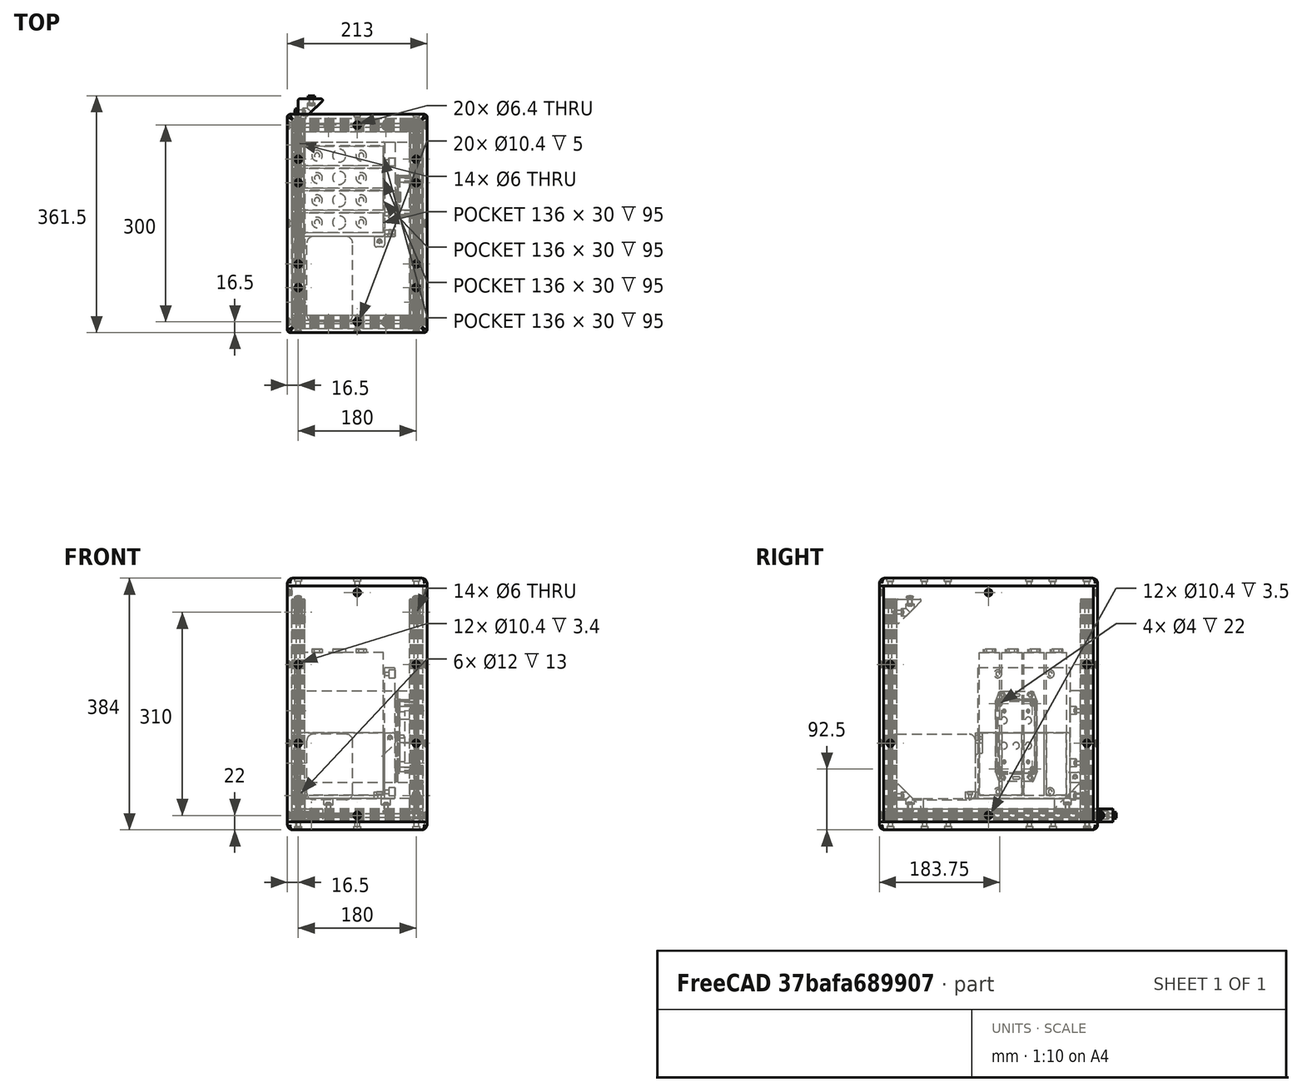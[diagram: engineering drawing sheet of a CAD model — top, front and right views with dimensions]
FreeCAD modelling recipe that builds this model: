
FCSTD DOCUMENT  (FreeCAD 0.17R9796 (Git))
Label: UPKframeNG2f
License: All rights reserved
LicenseURL: http://en.wikipedia.org/wiki/All_rights_reserved
objects: Part::Feature×70, Part::FeaturePython×24, Part::Compound×12, App::FeaturePython×8, App::Part×6, Part::Cylinder×5, Part::Box×4, Part::Cut×4, PartDesign::Body×2, PartDesign::Pocket×1, Part::Fillet×1, Part::MultiFuse×1
note: 125 computed .brp shape members not serialized (recipe doc carries the construction recipe); baked Part::Feature solids carry a one-line shape summary decoded from their .brp

FEATURE [Part::Feature] Pocket003001  label="tslot32con"
  Placement = pos=(0,10,10) rot=(1,0,0;1.5708rad)
  shape: bbox 20 x 320 x 20 mm, 150 faces (baked)
FEATURE [Part::Feature] Pocket003002  label="tslot16"
  Placement = pos=(10,0,10) rot=(0,1,0;1.5708rad)
  shape: bbox 160 x 20 x 20 mm, 94 faces (baked)
FEATURE [Part::Feature] Pocket003006  label="tslot16_001"
  Placement = pos=(10,-300,10) rot=(0,1,0;1.5708rad)
  shape: bbox 160 x 20 x 20 mm, 94 faces (baked)
FEATURE [Part::Feature] Pocket003007  label="tslot32con_001"
  Placement = pos=(180,-310,10) rot=(0,0.707107,0.707107;3.14159rad)
  shape: bbox 20 x 320 x 20 mm, 150 faces (baked)
FEATURE [Part::FeaturePython] Screw  label="M6x25-Screw"  # Fasteners workbench fastener (typed FeaturePython)
  Placement = pos=(-4,0,10) rot=(0,-1,0;1.5708rad)
  diameter = 7
  invert = false
  length = 6
  matchOuter = false
  offset = 0
  thread = false
  type = 15
FEATURE [Part::FeaturePython] Screw001  label="M6x25-Screw004"  # Fasteners workbench fastener (typed FeaturePython)
  Placement = pos=(-4,-300,10) rot=(0,-1,0;1.5708rad)
  diameter = 7
  invert = false
  length = 6
  matchOuter = false
  offset = 0
  thread = false
  type = 15
FEATURE [Part::FeaturePython] Screw002  label="M6x25-Screw005"  # Fasteners workbench fastener (typed FeaturePython)
  Placement = pos=(184,0,10) rot=(0,1,0;1.5708rad)
  diameter = 7
  invert = false
  length = 6
  matchOuter = false
  offset = 0
  thread = false
  type = 15
FEATURE [Part::FeaturePython] Screw004  label="M6x25-Screw006"  # Fasteners workbench fastener (typed FeaturePython)
  Placement = pos=(184,-300,10) rot=(0,1,0;1.5708rad)
  diameter = 7
  invert = false
  length = 6
  matchOuter = false
  offset = 0
  thread = false
  type = 15
FEATURE [App::Part] Part  label="lower_frame"
  Group = -> [Pocket003001,Pocket003002,Pocket003006,Pocket003007,Screw,Screw001,Screw002,Screw004]
  License = CC BY 3.0
  LicenseURL = http://creativecommons.org/licenses/by/3.0/
  Origin = -> PartOrigin
FEATURE [Part::Feature] Pocket003008  label="tslot32con001"
  Placement = pos=(0,10,10) rot=(1,0,0;1.5708rad)
  shape: bbox 20 x 320 x 20 mm, 150 faces (baked)
FEATURE [Part::Feature] Pocket003009  label="tslot041"
  Placement = pos=(10,0,10) rot=(0,1,0;1.5708rad)
  shape: bbox 160 x 20 x 20 mm, 94 faces (baked)
FEATURE [Part::Feature] Pocket003010  label="tslot16_002"
  Placement = pos=(10,-300,10) rot=(0,1,0;1.5708rad)
  shape: bbox 160 x 20 x 20 mm, 94 faces (baked)
FEATURE [Part::Feature] Pocket003011  label="tslot32con_002"
  Placement = pos=(180,-310,10) rot=(0,0.707107,0.707107;3.14159rad)
  shape: bbox 20 x 320 x 20 mm, 150 faces (baked)
FEATURE [Part::FeaturePython] Screw005  label="M6x25-Screw007"  # Fasteners workbench fastener (typed FeaturePython)
  Placement = pos=(-4,0,10) rot=(0,-1,0;1.5708rad)
  diameter = 7
  invert = false
  length = 6
  matchOuter = false
  offset = 0
  thread = false
  type = 15
FEATURE [Part::FeaturePython] Screw006  label="M6x25-Screw008"  # Fasteners workbench fastener (typed FeaturePython)
  Placement = pos=(-4,-300,10) rot=(0,-1,0;1.5708rad)
  diameter = 7
  invert = false
  length = 6
  matchOuter = false
  offset = 0
  thread = false
  type = 15
FEATURE [Part::FeaturePython] Screw007  label="M6x25-Screw009"  # Fasteners workbench fastener (typed FeaturePython)
  Placement = pos=(184,0,10) rot=(0,1,0;1.5708rad)
  diameter = 7
  invert = false
  length = 6
  matchOuter = false
  offset = 0
  thread = false
  type = 15
FEATURE [Part::FeaturePython] Screw008  label="M6x25-Screw010"  # Fasteners workbench fastener (typed FeaturePython)
  Placement = pos=(184,-300,10) rot=(0,1,0;1.5708rad)
  diameter = 7
  invert = false
  length = 6
  matchOuter = false
  offset = 0
  thread = false
  type = 15
FEATURE [App::Part] Part001  label="upper_frame"
  Group = -> [Pocket003008,Pocket003009,Pocket003010,Pocket003011,Screw005,Screw006,Screw007,Screw008]
  License = CC BY 3.0
  LicenseURL = http://creativecommons.org/licenses/by/3.0/
  Origin = -> PartOrigin001
  Placement = pos=(0,0,340) rot=(0,0,1;0rad)
FEATURE [Part::Feature] Fillet004001  label="Fillet005"
  shape: bbox 37.5 x 37.5 x 20 mm, 26 faces (baked)
FEATURE [Part::FeaturePython] Screw009  label="M6x12-Screw"  # Fasteners workbench fastener (typed FeaturePython)
  Placement = pos=(7,20,10) rot=(0,1,0;1.5708rad)
  diameter = 4
  invert = false
  length = 1
  matchOuter = false
  offset = 0
  thread = false
  type = 20
FEATURE [Part::Feature] Body001  label="m6nutplate"
  Placement = pos=(-1.5,15,5) rot=(0,-1,0;1.5708rad)
  shape: bbox 3 x 10 x 10 mm, 9 faces (baked)
FEATURE [App::Part] Part002  label="cornerstonescrewnut"
  License = CC BY 3.0
  LicenseURL = http://creativecommons.org/licenses/by/3.0/
  Origin = -> PartOrigin002
  Placement = pos=(10,-50,20) rot=(0,-1,0;1.5708rad)
FEATURE [Part::FeaturePython] Screw010  label="M6x12-Screw001"  # Fasteners workbench fastener (typed FeaturePython)
  Placement = pos=(20,33,10) rot=(1,0,0;1.5708rad)
  diameter = 4
  invert = false
  length = 1
  matchOuter = false
  offset = 0
  thread = false
  type = 20
FEATURE [Part::Feature] Body002  label="m6nutplate001"
  Placement = pos=(15,41.5,5) rot=(0.57735,0.57735,0.57735;4.18879rad)
  shape: bbox 10 x 3 x 10 mm, 9 faces (baked)
FEATURE [Part::Feature] Fillet004002  label="Fillet006"
  shape: bbox 37.5 x 37.5 x 20 mm, 26 faces (baked)
FEATURE [Part::FeaturePython] Screw011  label="M6x12-Screw002"  # Fasteners workbench fastener (typed FeaturePython)
  Placement = pos=(7,20,10) rot=(0,1,0;1.5708rad)
  diameter = 4
  invert = false
  length = 1
  matchOuter = false
  offset = 0
  thread = false
  type = 20
FEATURE [Part::Feature] Body003  label="m6nutplate002"
  Placement = pos=(-1.5,15,5) rot=(0,-1,0;1.5708rad)
  shape: bbox 3 x 10 x 10 mm, 9 faces (baked)
FEATURE [Part::FeaturePython] Screw012  label="M6x12-Screw003"  # Fasteners workbench fastener (typed FeaturePython)
  Placement = pos=(20,33,10) rot=(1,0,0;1.5708rad)
  diameter = 4
  invert = false
  length = 1
  matchOuter = false
  offset = 0
  thread = false
  type = 20
FEATURE [Part::Feature] Body004  label="m6nutplate003"
  Placement = pos=(15,41.5,5) rot=(0.57735,0.57735,0.57735;4.18879rad)
  shape: bbox 10 x 3 x 10 mm, 9 faces (baked)
FEATURE [App::Part] Part003  label="cornerstonescrewnut001"
  Group = -> [Body003,Screw011,Fillet004002,Screw012,Body004,PartOrigin002,Body001,Screw009,Fillet004001,Screw010,Body002,Part002]
  License = CC BY 3.0
  LicenseURL = http://creativecommons.org/licenses/by/3.0/
  Origin = -> PartOrigin003
  Placement = pos=(190,-50,20) rot=(0,-1,0;1.5708rad)
FEATURE [Part::Feature] Fillet004003  label="Fillet007"
  shape: bbox 37.5 x 37.5 x 20 mm, 26 faces (baked)
FEATURE [Part::FeaturePython] Screw013  label="M6x12-Screw004"  # Fasteners workbench fastener (typed FeaturePython)
  Placement = pos=(7,20,10) rot=(0,1,0;1.5708rad)
  diameter = 4
  invert = false
  length = 1
  matchOuter = false
  offset = 0
  thread = false
  type = 20
FEATURE [Part::Feature] Body005  label="m6nutplate004"
  Placement = pos=(-1.5,15,5) rot=(0,-1,0;1.5708rad)
  shape: bbox 3 x 10 x 10 mm, 9 faces (baked)
FEATURE [Part::FeaturePython] Screw014  label="M6x12-Screw005"  # Fasteners workbench fastener (typed FeaturePython)
  Placement = pos=(20,33,10) rot=(1,0,0;1.5708rad)
  diameter = 4
  invert = false
  length = 1
  matchOuter = false
  offset = 0
  thread = false
  type = 20
FEATURE [Part::Feature] Body006  label="m6nutplate005"
  Placement = pos=(15,41.5,5) rot=(0.57735,0.57735,0.57735;4.18879rad)
  shape: bbox 10 x 3 x 10 mm, 9 faces (baked)
FEATURE [App::Part] Part004  label="cornerstonescrewnut002"
  Group = -> [Body005,Screw013,Fillet004003,Screw014,Body006]
  License = CC BY 3.0
  LicenseURL = http://creativecommons.org/licenses/by/3.0/
  Origin = -> PartOrigin004
  Placement = pos=(-10,-50,340) rot=(0,1,0;1.5708rad)
FEATURE [Part::Feature] Fillet004004  label="Fillet008"
  shape: bbox 37.5 x 37.5 x 20 mm, 26 faces (baked)
FEATURE [Part::FeaturePython] Screw015  label="M6x12-Screw006"  # Fasteners workbench fastener (typed FeaturePython)
  Placement = pos=(7,20,10) rot=(0,1,0;1.5708rad)
  diameter = 4
  invert = false
  length = 1
  matchOuter = false
  offset = 0
  thread = false
  type = 20
FEATURE [Part::Feature] Body007  label="m6nutplate006"
  Placement = pos=(-1.5,15,5) rot=(0,-1,0;1.5708rad)
  shape: bbox 3 x 10 x 10 mm, 9 faces (baked)
FEATURE [Part::FeaturePython] Screw016  label="M6x12-Screw007"  # Fasteners workbench fastener (typed FeaturePython)
  Placement = pos=(20,33,10) rot=(1,0,0;1.5708rad)
  diameter = 4
  invert = false
  length = 1
  matchOuter = false
  offset = 0
  thread = false
  type = 20
FEATURE [Part::Feature] Body008  label="m6nutplate007"
  Placement = pos=(15,41.5,5) rot=(0.57735,0.57735,0.57735;4.18879rad)
  shape: bbox 10 x 3 x 10 mm, 9 faces (baked)
FEATURE [App::Part] Part005  label="cornerstonescrewnut003"
  Group = -> [Body007,Screw015,Fillet004004,Screw016,Body008]
  License = CC BY 3.0
  LicenseURL = http://creativecommons.org/licenses/by/3.0/
  Origin = -> PartOrigin005
  Placement = pos=(170,-50,340) rot=(0,1,0;1.5708rad)
FEATURE [Part::Feature] Body009001  label="m6nutplate010"
  Placement = pos=(-1.5,15,5) rot=(0,-1,0;1.5708rad)
  shape: bbox 3 x 10 x 10 mm, 9 faces (baked)
FEATURE [Part::Feature] Body010001  label="m6nutplate011"
  Placement = pos=(15,41.5,5) rot=(0.57735,0.57735,0.57735;4.18879rad)
  shape: bbox 10 x 3 x 10 mm, 9 faces (baked)
FEATURE [Part::Feature] Screw018001  label="M6x12-Screw010"
  Placement = pos=(20,33,10) rot=(1,0,0;1.5708rad)
  shape: bbox 10.5 x 15.3 x 10.5 mm, 15 faces (baked)
FEATURE [Part::Feature] Screw017001  label="M6x12-Screw011"
  Placement = pos=(7,20,10) rot=(0,1,0;1.5708rad)
  shape: bbox 15.3 x 10.5 x 10.5 mm, 15 faces (baked)
FEATURE [Part::Feature] Fillet004005001  label="Fillet010"
  shape: bbox 37.5 x 37.5 x 20 mm, 26 faces (baked)
FEATURE [Part::Compound] Compound
  Links = -> [Body009001,Fillet004005001,Screw017001,Body010001,Screw018001]
  Placement = pos=(10,-250,340) rot=(0.707107,0,-0.707107;3.14159rad)
FEATURE [Part::Feature] Body010002  label="m6nutplate012"
  Placement = pos=(-1.5,15,5) rot=(0,-1,0;1.5708rad)
  shape: bbox 3 x 10 x 10 mm, 9 faces (baked)
FEATURE [Part::Feature] Body010003  label="m6nutplate013"
  Placement = pos=(15,41.5,5) rot=(0.57735,0.57735,0.57735;4.18879rad)
  shape: bbox 10 x 3 x 10 mm, 9 faces (baked)
FEATURE [Part::Feature] Screw018002  label="M6x12-Screw012"
  Placement = pos=(20,33,10) rot=(1,0,0;1.5708rad)
  shape: bbox 10.5 x 15.3 x 10.5 mm, 15 faces (baked)
FEATURE [Part::Feature] Screw018003  label="M6x12-Screw013"
  Placement = pos=(7,20,10) rot=(0,1,0;1.5708rad)
  shape: bbox 15.3 x 10.5 x 10.5 mm, 15 faces (baked)
FEATURE [Part::Feature] Fillet004005002  label="Fillet011"
  shape: bbox 37.5 x 37.5 x 20 mm, 26 faces (baked)
FEATURE [Part::Compound] Compound001
  Links = -> [Body010002,Fillet004005002,Screw018003,Body010003,Screw018002]
  Placement = pos=(190,-250,340) rot=(0.707107,0,-0.707107;3.14159rad)
FEATURE [Part::Feature] Body010004  label="m6nutplate014"
  Placement = pos=(-1.5,15,5) rot=(0,-1,0;1.5708rad)
  shape: bbox 3 x 10 x 10 mm, 9 faces (baked)
FEATURE [Part::Feature] Body010005  label="m6nutplate015"
  Placement = pos=(15,41.5,5) rot=(0.57735,0.57735,0.57735;4.18879rad)
  shape: bbox 10 x 3 x 10 mm, 9 faces (baked)
FEATURE [Part::Feature] Screw018004  label="M6x12-Screw014"
  Placement = pos=(20,33,10) rot=(1,0,0;1.5708rad)
  shape: bbox 10.5 x 15.3 x 10.5 mm, 15 faces (baked)
FEATURE [Part::Feature] Screw018005  label="M6x12-Screw015"
  Placement = pos=(7,20,10) rot=(0,1,0;1.5708rad)
  shape: bbox 15.3 x 10.5 x 10.5 mm, 15 faces (baked)
FEATURE [Part::Feature] Fillet004005003  label="Fillet012"
  shape: bbox 37.5 x 37.5 x 20 mm, 26 faces (baked)
FEATURE [Part::Compound] Compound002
  Links = -> [Body010004,Fillet004005003,Screw018005,Body010005,Screw018004]
  Placement = pos=(10,-290,60) rot=(0.57735,0.57735,-0.57735;4.18879rad)
FEATURE [Part::Feature] Body010006  label="m6nutplate016"
  Placement = pos=(-1.5,15,5) rot=(0,-1,0;1.5708rad)
  shape: bbox 3 x 10 x 10 mm, 9 faces (baked)
FEATURE [Part::Feature] Body010007  label="m6nutplate017"
  Placement = pos=(15,41.5,5) rot=(0.57735,0.57735,0.57735;4.18879rad)
  shape: bbox 10 x 3 x 10 mm, 9 faces (baked)
FEATURE [Part::Feature] Screw018006  label="M6x12-Screw016"
  Placement = pos=(20,33,10) rot=(1,0,0;1.5708rad)
  shape: bbox 10.5 x 15.3 x 10.5 mm, 15 faces (baked)
FEATURE [Part::Feature] Screw018007  label="M6x12-Screw017"
  Placement = pos=(7,20,10) rot=(0,1,0;1.5708rad)
  shape: bbox 15.3 x 10.5 x 10.5 mm, 15 faces (baked)
FEATURE [Part::Feature] Fillet004005004  label="Fillet013"
  shape: bbox 37.5 x 37.5 x 20 mm, 26 faces (baked)
FEATURE [Part::Compound] Compound003
  Links = -> [Body010006,Fillet004005004,Screw018007,Body010007,Screw018006]
  Placement = pos=(190,-290,60) rot=(0.57735,0.57735,-0.57735;4.18879rad)
FEATURE [Part::Feature] Pocket001001  label="tslot32"
  Placement = pos=(0,0,20) rot=(0,0,1;0rad)
  shape: bbox 20 x 20 x 320 mm, 94 faces (baked)
FEATURE [Part::Feature] Body010008  label="m6nutplate018"
  Placement = pos=(-1.5,15,5) rot=(0,-1,0;1.5708rad)
  shape: bbox 3 x 10 x 10 mm, 9 faces (baked)
FEATURE [Part::Feature] Body010009  label="m6nutplate019"
  Placement = pos=(15,41.5,5) rot=(0.57735,0.57735,0.57735;4.18879rad)
  shape: bbox 10 x 3 x 10 mm, 9 faces (baked)
FEATURE [Part::Feature] Screw018008  label="M6x12-Screw018"
  Placement = pos=(20,33,10) rot=(1,0,0;1.5708rad)
  shape: bbox 10.5 x 15.3 x 10.5 mm, 15 faces (baked)
FEATURE [Part::Feature] Screw018009  label="M6x12-Screw019"
  Placement = pos=(7,20,10) rot=(0,1,0;1.5708rad)
  shape: bbox 15.3 x 10.5 x 10.5 mm, 15 faces (baked)
FEATURE [Part::Feature] Fillet004005005  label="Fillet014"
  shape: bbox 37.5 x 37.5 x 20 mm, 26 faces (baked)
FEATURE [Part::Compound] Compound004
  Links = -> [Body010008,Fillet004005005,Screw018009,Body010009,Screw018008]
  Placement = pos=(-10,-10,60) rot=(0.57735,-0.57735,0.57735;4.18879rad)
FEATURE [Part::Feature] Pocket003012  label="tslot32_001"
  Placement = pos=(0,-300,20) rot=(0,0,1;0rad)
  shape: bbox 20 x 20 x 320 mm, 94 faces (baked)
FEATURE [Part::Feature] Pocket003013  label="tslot32_002"
  Placement = pos=(180,0,20) rot=(0,0,1;0rad)
  shape: bbox 20 x 20 x 320 mm, 94 faces (baked)
FEATURE [Part::Feature] Pocket003014  label="tslot32_003"
  Placement = pos=(180,-300,20) rot=(0,0,1;0rad)
  shape: bbox 20 x 20 x 320 mm, 94 faces (baked)
FEATURE [PartDesign::Body] Body010027
FEATURE [Part::FeaturePython] Screw018021  label="M6x12-Screw032"  # Fasteners workbench fastener (typed FeaturePython)
  diameter = 4
  invert = false
  length = 1
  matchOuter = false
  offset = 0
  thread = false
  type = 20
FEATURE [Part::Feature] Body010028  label="m6nutplate032"
  Placement = pos=(5,-5,-8.39) rot=(0,1,0;3.14159rad)
  shape: bbox 10 x 10 x 3 mm, 9 faces (baked)
FEATURE [App::FeaturePython] circularEdgeConstraint009  # a2plus constraint (typed FeaturePython)
  Object1 = Screw
  Object2 = Body001
  SubElement1 = Edge7
  SubElement2 = Edge20
  Type = circularEdge
  directionConstraint = 1
  lockRotation = false
  offset = 0
FEATURE [Part::Compound] Compound017  label="nutplate12screw008"
  Links = -> [Screw018021,circularEdgeConstraint009,Body010028]
  Placement = pos=(10,30,6) rot=(0,0,1;0rad)
FEATURE [Part::FeaturePython] Screw018022  label="M6x12-Screw033"  # Fasteners workbench fastener (typed FeaturePython)
  diameter = 4
  invert = false
  length = 1
  matchOuter = false
  offset = 0
  thread = false
  type = 20
FEATURE [Part::Feature] Body010029  label="m6nutplate033"
  Placement = pos=(5,-5,-8.39) rot=(0,1,0;3.14159rad)
  shape: bbox 10 x 10 x 3 mm, 9 faces (baked)
FEATURE [App::FeaturePython] circularEdgeConstraint010  # a2plus constraint (typed FeaturePython)
  Object1 = Screw
  Object2 = Body001
  SubElement1 = Edge7
  SubElement2 = Edge20
  Type = circularEdge
  directionConstraint = 1
  lockRotation = false
  offset = 0
FEATURE [Part::Compound] Compound018  label="nutplate12screw009"
  Links = -> [Screw018022,circularEdgeConstraint010,Body010029]
  Placement = pos=(10,110,6) rot=(0,0,1;0rad)
FEATURE [Part::FeaturePython] Screw018023  label="M6x12-Screw034"  # Fasteners workbench fastener (typed FeaturePython)
  diameter = 4
  invert = false
  length = 1
  matchOuter = false
  offset = 0
  thread = false
  type = 20
FEATURE [Part::Feature] Body010030  label="m6nutplate034"
  Placement = pos=(5,-5,-8.39) rot=(0,1,0;3.14159rad)
  shape: bbox 10 x 10 x 3 mm, 9 faces (baked)
FEATURE [App::FeaturePython] circularEdgeConstraint011  # a2plus constraint (typed FeaturePython)
  Object1 = Screw
  Object2 = Body001
  SubElement1 = Edge7
  SubElement2 = Edge20
  Type = circularEdge
  directionConstraint = 1
  lockRotation = false
  offset = 0
FEATURE [Part::Compound] Compound019  label="nutplate12screw010"
  Links = -> [Screw018023,circularEdgeConstraint011,Body010030]
  Placement = pos=(190,110,6) rot=(0,0,1;0rad)
FEATURE [Part::FeaturePython] Screw018024  label="M6x12-Screw035"  # Fasteners workbench fastener (typed FeaturePython)
  diameter = 4
  invert = false
  length = 1
  matchOuter = false
  offset = 0
  thread = false
  type = 20
FEATURE [Part::Feature] Body010031  label="m6nutplate035"
  Placement = pos=(5,-5,-8.39) rot=(0,1,0;3.14159rad)
  shape: bbox 10 x 10 x 3 mm, 9 faces (baked)
FEATURE [App::FeaturePython] circularEdgeConstraint012  # a2plus constraint (typed FeaturePython)
  Object1 = Screw
  Object2 = Body001
  SubElement1 = Edge7
  SubElement2 = Edge20
  Type = circularEdge
  directionConstraint = 1
  lockRotation = false
  offset = 0
FEATURE [Part::Compound] Compound020  label="nutplate12screw011"
  Links = -> [Screw018024,circularEdgeConstraint012,Body010031]
  Placement = pos=(190,30,6) rot=(0,0,1;0rad)
FEATURE [Part::Compound] Compound021  label="front_plate"
  Links = -> [Body010027,Compound020,Compound019,Compound017,Compound018]
  Placement = pos=(-10,-10,60) rot=(1,0,0;1.5708rad)
FEATURE [Part::Compound] Compound016  label="bottom_plate"
  Placement = pos=(190,-310,20) rot=(0,0,1;1.5708rad)
FEATURE [PartDesign::Pocket] Pocket003019
  Length = 10
  Placement = pos=(130,-166,235) rot=(0,1,0;1.5708rad)
  Type = 0
FEATURE [Part::Box] Box003  label="MPPT"
  AttacherType = Attacher::AttachEngine3D
  Height = 100
  Length = 130
  Placement = pos=(290,128,10) rot=(0,0,1;0rad)
  Width = 70
FEATURE [Part::Fillet] Fillet007  label="MPPT               "
  Base = -> Box003
  Edges = 12 edges r=10: [Edge1,Edge2,Edge3,Edge4,Edge5,Edge6,Edge7,Edge8,Edge9,Edge10,Edge11,Edge12]
  Placement = pos=(211,-590,24) rot=(0,0,1;1.5708rad)
FEATURE [Part::Feature] Part__Feature1213  label="1591XXBF LID"
  Placement = pos=(153,-86,180) rot=(-0.57735,0.57735,0.57735;4.18879rad)
  shape: bbox 12.61 x 63.32 x 138 mm, 220 faces (baked)
FEATURE [Part::Feature] Part__Feature1212  label="1591XXB BOX"
  Placement = pos=(0,0,0) rot=(0,0.707107,0.707107;3.14159rad)
  shape: bbox 113.8 x 28.25 x 63.32 mm, 133 faces (baked)
FEATURE [Part::Cylinder] Cylinder  label="Zylinder"
  Angle = 360
  AttacherType = Attacher::AttachEngine3D
  Height = 60
  Placement = pos=(-14,48,18.6) rot=(1,0,0;1.5708rad)
  Radius = 5
FEATURE [Part::Cylinder] Cylinder001  label="Zylinder001"
  Angle = 360
  AttacherType = Attacher::AttachEngine3D
  Height = 60
  Placement = pos=(-14,48,0) rot=(1,0,0;1.5708rad)
  Radius = 5
FEATURE [Part::Cylinder] Cylinder002  label="Zylinder002"
  Angle = 360
  AttacherType = Attacher::AttachEngine3D
  Height = 60
  Placement = pos=(-14,48,-18.66) rot=(1,0,0;1.5708rad)
  Radius = 5
FEATURE [Part::Cylinder] Cylinder003  label="Zylinder003"
  Angle = 360
  AttacherType = Attacher::AttachEngine3D
  Height = 60
  Placement = pos=(24.49,48,18.6) rot=(1,0,0;1.5708rad)
  Radius = 5
FEATURE [Part::Cylinder] Cylinder004  label="Zylinder004"
  Angle = 360
  AttacherType = Attacher::AttachEngine3D
  Height = 60
  Placement = pos=(24.49,48,-18.66) rot=(1,0,0;1.5708rad)
  Radius = 5
FEATURE [Part::MultiFuse] Fusion
  Shapes = -> [Cylinder,Cylinder004,Cylinder003,Cylinder002,Cylinder001]
FEATURE [Part::Cut] Cut
  Base = -> Part__Feature1212
  Tool = -> Fusion
FEATURE [Part::Box] Box002  label="Würfel002"
  AttacherType = Attacher::AttachEngine3D
  Height = 10
  Length = 76
  Placement = pos=(-38,16,-36) rot=(0,0,1;0rad)
  Width = 12.6
FEATURE [Part::Cut] Cut001
  Base = -> Cut
  Tool = -> Box002
FEATURE [Part::Box] Box004  label="Würfel003"
  AttacherType = Attacher::AttachEngine3D
  Height = 10
  Length = 36
  Placement = pos=(-10,9,24) rot=(0,0,1;0rad)
  Width = 20
FEATURE [Part::Cut] Cut002
  Base = -> Cut001
  Tool = -> Box004
FEATURE [Part::Box] Box  label="Würfel"
  AttacherType = Attacher::AttachEngine3D
  Height = 20
  Length = 10
  Placement = pos=(49,23,-6) rot=(0,0,1;0rad)
  Width = 6
FEATURE [Part::Cut] Cut003  label="bms-cover"
  Base = -> Cut002
  Placement = pos=(179,-108,130.5) rot=(0.57735,-0.57735,0.57735;2.0944rad)
  Tool = -> Box
FEATURE [PartDesign::Body] Body010032
FEATURE [Part::FeaturePython] Screw018025  label="M6x12-Screw036"  # Fasteners workbench fastener (typed FeaturePython)
  diameter = 4
  invert = false
  length = 1
  matchOuter = false
  offset = 0
  thread = false
  type = 20
FEATURE [App::FeaturePython] circularEdgeConstraint013  # a2plus constraint (typed FeaturePython)
  Object1 = Screw
  Object2 = Body001
  SubElement1 = Edge7
  SubElement2 = Edge20
  Type = circularEdge
  directionConstraint = 1
  lockRotation = false
  offset = 0
FEATURE [Part::FeaturePython] Screw018026  label="M6x12-Screw037"  # Fasteners workbench fastener (typed FeaturePython)
  diameter = 4
  invert = false
  length = 1
  matchOuter = false
  offset = 0
  thread = false
  type = 20
FEATURE [Part::Feature] Body010034  label="m6nutplate037"
  Placement = pos=(5,-5,-8.39) rot=(0,1,0;3.14159rad)
  shape: bbox 10 x 10 x 3 mm, 9 faces (baked)
FEATURE [App::FeaturePython] circularEdgeConstraint014  # a2plus constraint (typed FeaturePython)
  Object1 = Screw
  Object2 = Body001
  SubElement1 = Edge7
  SubElement2 = Edge20
  Type = circularEdge
  directionConstraint = 1
  lockRotation = false
  offset = 0
FEATURE [Part::FeaturePython] Screw018027  label="M6x12-Screw038"  # Fasteners workbench fastener (typed FeaturePython)
  diameter = 4
  invert = false
  length = 1
  matchOuter = false
  offset = 0
  thread = false
  type = 20
FEATURE [Part::Feature] Body010035  label="m6nutplate038"
  Placement = pos=(5,-5,-8.39) rot=(0,1,0;3.14159rad)
  shape: bbox 10 x 10 x 3 mm, 9 faces (baked)
FEATURE [App::FeaturePython] circularEdgeConstraint015  # a2plus constraint (typed FeaturePython)
  Object1 = Screw
  Object2 = Body001
  SubElement1 = Edge7
  SubElement2 = Edge20
  Type = circularEdge
  directionConstraint = 1
  lockRotation = false
  offset = 0
FEATURE [Part::FeaturePython] Screw018028  label="M6x12-Screw039"  # Fasteners workbench fastener (typed FeaturePython)
  diameter = 4
  invert = false
  length = 1
  matchOuter = false
  offset = 0
  thread = false
  type = 20
FEATURE [Part::Feature] Body010036  label="m6nutplate039"
  Placement = pos=(5,-5,-8.39) rot=(0,1,0;3.14159rad)
  shape: bbox 10 x 10 x 3 mm, 9 faces (baked)
FEATURE [App::FeaturePython] circularEdgeConstraint016  # a2plus constraint (typed FeaturePython)
  Object1 = Screw
  Object2 = Body001
  SubElement1 = Edge7
  SubElement2 = Edge20
  Type = circularEdge
  directionConstraint = 1
  lockRotation = false
  offset = 0
FEATURE [Part::Compound] Compound026  label="bmsmounting_plate"
  Links = -> [Body010032]
  Placement = pos=(132,-26,36) rot=(0.707107,0,0.707107;3.14159rad)
FEATURE [Part::Feature] Body010037  label="batterymount"
  Placement = pos=(-10,-170,36) rot=(0,0,1;0rad)
  shape: bbox 158 x 176 x 100 mm, 72 faces (baked)
FEATURE [Part::Feature] Body010033  label="m6nutplate036"
  Placement = pos=(5,-5,-8.39) rot=(0,1,0;3.14159rad)
  shape: bbox 10 x 10 x 3 mm, 9 faces (baked)
FEATURE [Part::Feature] Body010038  label="cam72"
  Placement = pos=(130,-62,41) rot=(0,0,1;1.5708rad)
  shape: bbox 135.1 x 31 x 222.5 mm, 16 faces (baked)
FEATURE [Part::Feature] Body010039  label="cam72_001"
  Placement = pos=(130,-96,41) rot=(0,0,1;1.5708rad)
  shape: bbox 135.1 x 31 x 222.5 mm, 16 faces (baked)
FEATURE [Part::Feature] Body010040  label="cam72_002"
  Placement = pos=(130,-130,41) rot=(0,0,1;1.5708rad)
  shape: bbox 135.1 x 31 x 222.5 mm, 16 faces (baked)
FEATURE [Part::Feature] Body010041  label="cam72_003"
  Placement = pos=(130,-164,41) rot=(0,0,1;1.5708rad)
  shape: bbox 135.1 x 31 x 222.5 mm, 16 faces (baked)
FEATURE [Part::Feature] Body010042  label="backCover"
  Placement = pos=(-16.5,-310,0) rot=(1,0,0;1.5708rad)
  shape: bbox 213 x 6.5 x 360 mm, 26 faces (baked)
FEATURE [Part::Feature] Body010043  label="frontCover"
  Placement = pos=(196.5,10,0) rot=(0,0.707107,0.707107;3.14159rad)
  shape: bbox 213 x 6.5 x 360 mm, 26 faces (baked)
FEATURE [Part::Feature] Body010044  label="topCover"
  Placement = pos=(-16.5,-316.5,360) rot=(0,0,1;0rad)
  shape: bbox 213 x 333 x 12 mm, 48 faces (baked)
FEATURE [Part::Feature] Body010045  label="bottomCover"
  Placement = pos=(196.5,-316.5,0) rot=(0,1,0;3.14159rad)
  shape: bbox 213 x 333 x 12 mm, 48 faces (baked)
FEATURE [Part::Feature] Pocket003020  label="sideCover"
  Placement = pos=(190,-310,0) rot=(0.57735,0.57735,0.57735;2.0944rad)
  shape: bbox 6.5 x 320 x 360 mm, 24 faces (baked)
FEATURE [Part::Feature] Pocket003021  label="sideCover001"
  Placement = pos=(-10,10,0) rot=(-0.57735,0.57735,0.57735;4.18879rad)
  shape: bbox 6.5 x 320 x 360 mm, 24 faces (baked)
